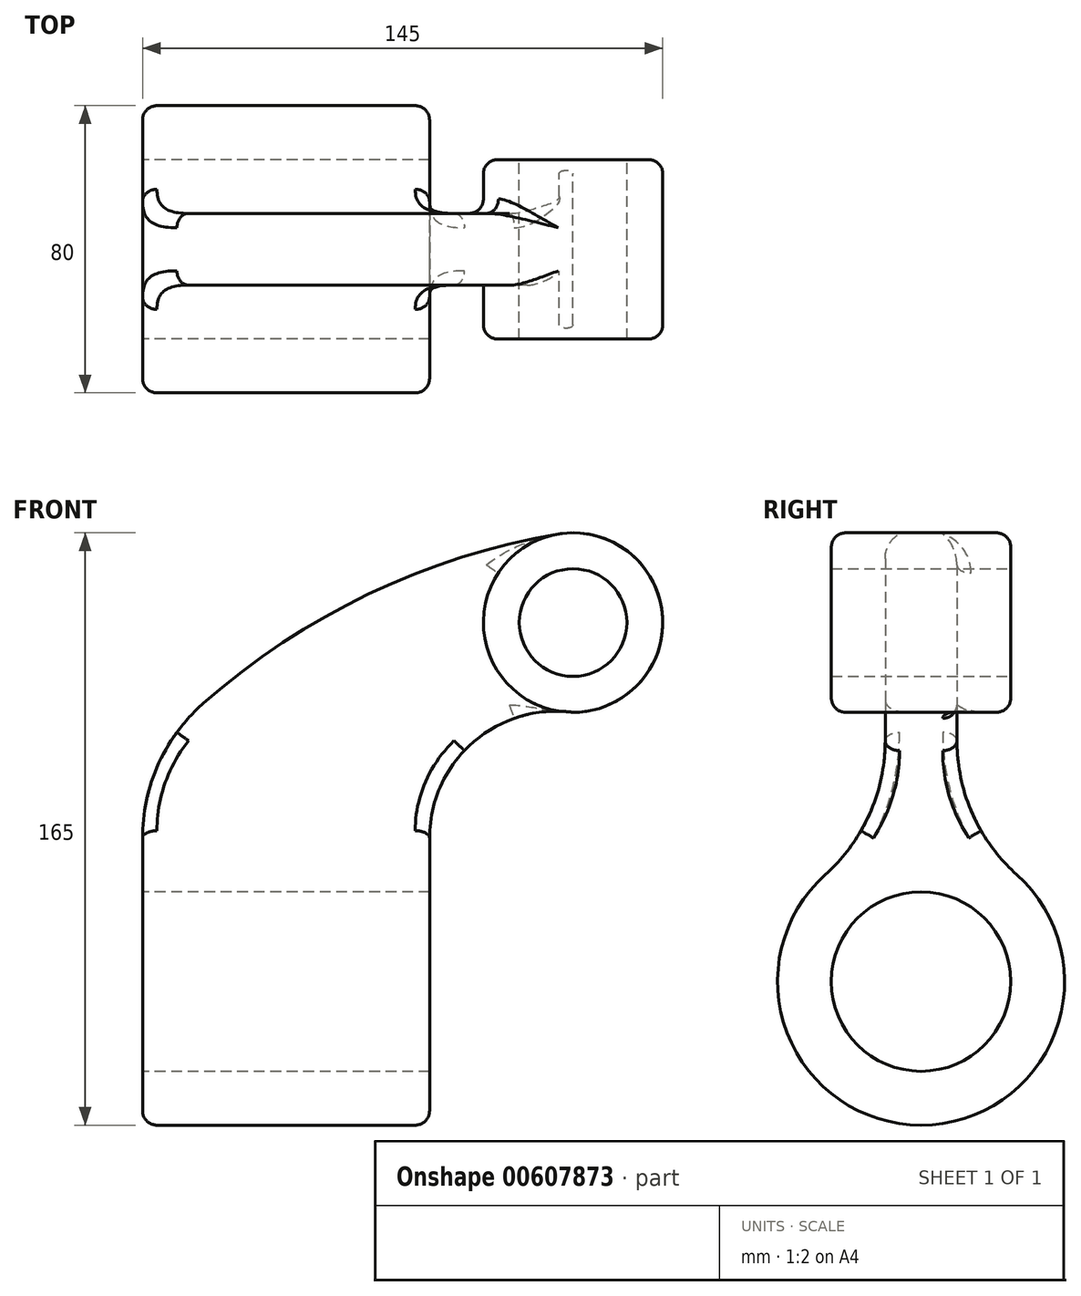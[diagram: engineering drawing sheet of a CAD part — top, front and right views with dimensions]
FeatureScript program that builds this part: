
annotation { "Feature Type Name" : "Feature", "Feature Type Description" : "" }
export const myFeature = defineFeature(function(context is Context, id is Id, definition is map)
    precondition{}
    {
        {
            var Q0;
            Q0=qCreatedBy(makeId("Front.planeOp"),FACE);
            var sketch = newSketch(context, id + "F0", { "sketchPlane" : qUnion([Q0])});
            skLineSegment(sketch, "E0", {"start": v(-99.17, 0) * mm, "end": v(0, 0) * mm, "construction": true});
            skLineSegment(sketch, "E1", {"start": v(-80, 25) * mm, "end": v(0, 25) * mm});
            skLineSegment(sketch, "E2", {"start": v(0, 40) * mm, "end": v(-80, 40) * mm});
            skLineSegment(sketch, "E3", {"start": v(-80, 40) * mm, "end": v(-80, 25) * mm});
            skLineSegment(sketch, "E4", {"start": v(0, 40) * mm, "end": v(0, 25) * mm});
            skCircle(sketch, "E5", {"center": v(40, 100) * mm, "radius": 15 * mm});
            skCircle(sketch, "E6", {"center": v(40, 100) * mm, "radius": 25 * mm});
            skLineSegment(sketch, "E7", {"start": v(40, 100) * mm, "end": v(40, 0) * mm});
            skLineSegment(sketch, "E8", {"start": v(40, 0) * mm, "end": v(37.86, -0.52) * mm});
            skArc(sketch, "E9", {"start": v(40, 75) * mm, "mid": v(12.06, 66.58) * mm, "end": v(0, 40) * mm});
            skArc(sketch, "E10", {"start": v(-80, 40) * mm, "mid": v(-75.57, 60.58) * mm, "end": v(-63.05, 77.52) * mm});
            skArc(sketch, "E11", {"start": v(-63.05, 77.52) * mm, "mid": v(-16.9, 107.99) * mm, "end": v(35.84, 124.65) * mm});
            skSolve(sketch);
        }
        {
            var Q0;
            Q0=makeQuery(id+"F0.imprint","IMPRINT",FACE,{"disambiguationData":[TD([[makeQuery(id+"F0.imprint","IMPRINT",EDGE,{"derivedFrom":sQuery(id+"F0.wireOp",EDGE,"E1")}),1.0]])]});
            var Q1;
            Q1=sQuery(id+"F0.wireOp",EDGE,"E0");
            revolve(context, id + "F1", {"entities" : qUnion([Q0]), "axis" : qUnion([Q1]), "revolveType" : RevolveType.FULL});
        }
        {
            var Q0;
            {var subQ1=sQuery(id+"F0.wireOp",EDGE,"E2");Q0=makeQuery(id+"F0.imprint","IMPRINT",FACE,{"disambiguationData":[TD([[makeQuery(id+"F0.imprint","IMPRINT",EDGE,{"derivedFrom":subQ1}),-1.0]])]});}
            extrude(context, id + "F2", {"entities" : qUnion([Q0]), "operationType" : NewBodyOperationType.ADD, "endBound" : BoundingType.SYMMETRIC, "depth" : 20 * mm, "offsetDistance" : 25 * mm});
        }
        {
            var Q0;
            Q0=makeQuery(id+"F0.imprint","IMPRINT",FACE,{"disambiguationData":[TD([[makeQuery(id+"F0.imprint","IMPRINT",EDGE,{"derivedFrom":sQuery(id+"F0.wireOp",EDGE,"E5")}),-1.0]])]});
            extrude(context, id + "F3", {"entities" : qUnion([Q0]), "operationType" : NewBodyOperationType.ADD, "endBound" : BoundingType.SYMMETRIC, "depth" : 50 * mm, "offsetDistance" : 25 * mm});
        }
        {
            var Q0;
            Q0=makeQuery(id+"F0.imprint","IMPRINT",FACE,{"disambiguationData":[TD([[makeQuery(id+"F0.imprint","IMPRINT",EDGE,{"derivedFrom":sQuery(id+"F0.wireOp",EDGE,"E1")}),1.0]])]});
            extrude(context, id + "F4", {"entities" : qUnion([Q0]), "operationType" : NewBodyOperationType.ADD, "endBound" : BoundingType.SYMMETRIC, "depth" : 20 * mm, "offsetDistance" : 25 * mm});
        }
        {
            var Q0;
            {var subQ0=sQuery(id+"F0.wireOp",EDGE,"E2");Q0=makeQuery(id+"F4.boolean.opBoolean","INTERSECT",EDGE,{"derivedFrom":[makeQuery(id+"F1.opRevolve","SWEPT_FACE",FACE,{"disambiguationData":[OSD([subQ0])]}),makeQuery(id+"F4.opExtrude","CAP_FACE",FACE,{"disambiguationData":[OSD([sQuery(id+"F0.wireOp",EDGE,"E1"),subQ0,sQuery(id+"F0.wireOp",EDGE,"E3"),sQuery(id+"F0.wireOp",EDGE,"E4")])],"isStart":false})]});}
            var Q1;
            {var subQ0=sQuery(id+"F0.wireOp",EDGE,"E2");Q1=makeQuery(id+"F4.boolean.opBoolean","INTERSECT",EDGE,{"derivedFrom":[makeQuery(id+"F1.opRevolve","SWEPT_FACE",FACE,{"disambiguationData":[OSD([subQ0])]}),makeQuery(id+"F4.opExtrude","CAP_FACE",FACE,{"disambiguationData":[OSD([sQuery(id+"F0.wireOp",EDGE,"E1"),subQ0,sQuery(id+"F0.wireOp",EDGE,"E3"),sQuery(id+"F0.wireOp",EDGE,"E4")])],"isStart":true})]});}
            fillet(context, id + "F5", {"entities" : qUnion([Q0, Q1]), "radius" : 50 * mm, "tangentPropagation" : true, "allowEdgeOverflow" : false});
        }
        {
            var Q0;
            Q0=makeQuery(id+"F3.opExtrude","CAP_EDGE",EDGE,{"disambiguationData":[OSD([sQuery(id+"F0.wireOp",EDGE,"E6")])],"isStart":false});
            var Q1;
            Q1=makeQuery(id+"F3.opExtrude","CAP_EDGE",EDGE,{"disambiguationData":[OSD([sQuery(id+"F0.wireOp",EDGE,"E6")])],"isStart":true});
            fillet(context, id + "F6", {"entities" : qUnion([Q0, Q1]), "radius" : 4 * mm, "tangentPropagation" : true, "allowEdgeOverflow" : false});
        }
        {
            var Q0;
            Q0=makeQuery(id+"F2.opExtrude","CAP_EDGE",EDGE,{"disambiguationData":[OSD([sQuery(id+"F0.wireOp",EDGE,"E11")])],"isStart":false});
            var Q1;
            {var subQ0=sQuery(id+"F0.wireOp",EDGE,"E2");Q1=makeQuery(id+"F4.boolean.opBoolean","MERGE",FACE,{"derivedFrom":[makeQuery(id+"F2.opExtrude","CAP_FACE",FACE,{"disambiguationData":[OSD([subQ0,sQuery(id+"F0.wireOp",EDGE,"E6"),sQuery(id+"F0.wireOp",EDGE,"E9"),sQuery(id+"F0.wireOp",EDGE,"E10"),sQuery(id+"F0.wireOp",EDGE,"E11")])],"isStart":true}),makeQuery(id+"F4.opExtrude","CAP_FACE",FACE,{"disambiguationData":[OSD([sQuery(id+"F0.wireOp",EDGE,"E1"),subQ0,sQuery(id+"F0.wireOp",EDGE,"E3"),sQuery(id+"F0.wireOp",EDGE,"E4")])],"isStart":true})]});}
            fillet(context, id + "F7", {"entities" : qUnion([Q0, Q1]), "radius" : 4 * mm, "tangentPropagation" : true, "allowEdgeOverflow" : false});
        }
    });
